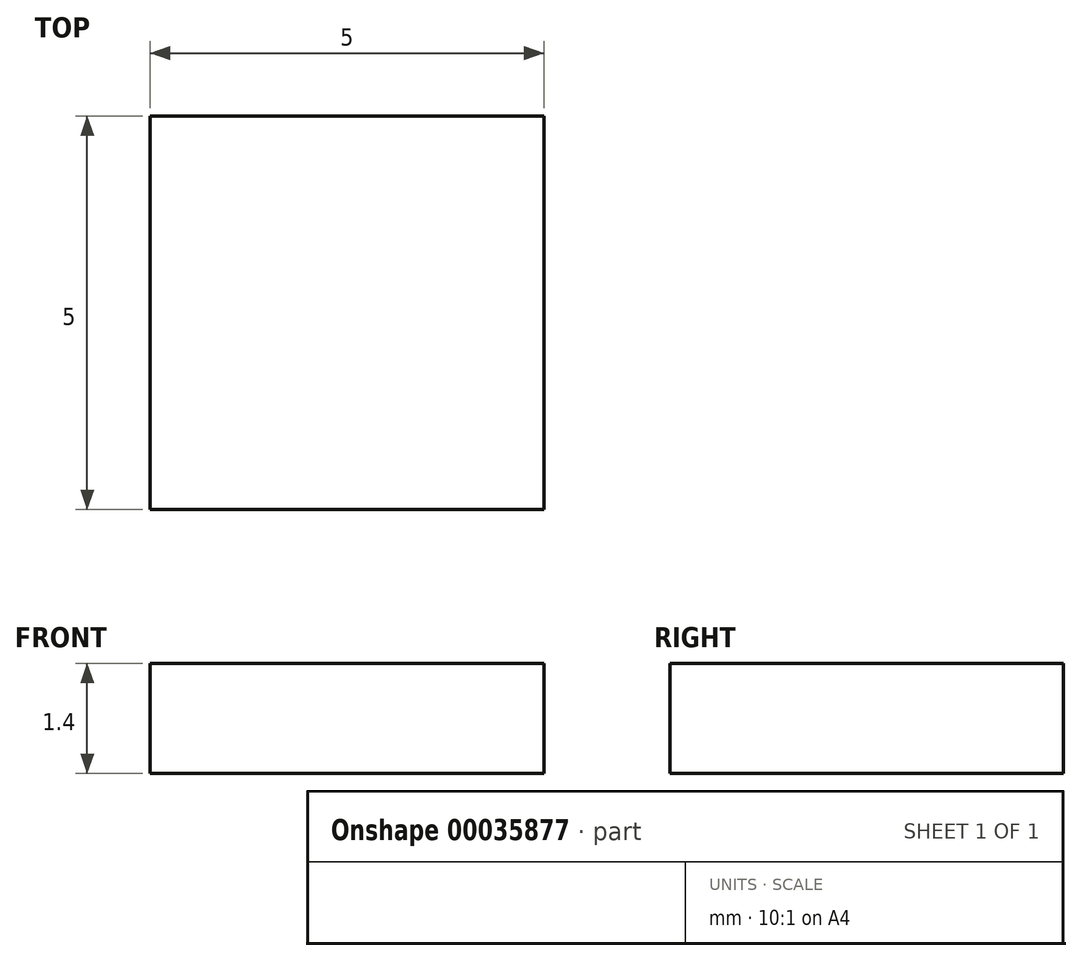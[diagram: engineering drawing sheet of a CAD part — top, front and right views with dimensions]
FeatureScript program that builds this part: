
annotation { "Feature Type Name" : "Feature", "Feature Type Description" : "" }
export const myFeature = defineFeature(function(context is Context, id is Id, definition is map)
    precondition{}
    {
        {
            var Q0;
            Q0=qCreatedBy(makeId("Top.planeOp"),FACE);
            var sketch = newSketch(context, id + "F0", { "sketchPlane" : qUnion([Q0])});
            skLineSegment(sketch, "E0.bottom", {"start": v(0, 0) * mm, "end": v(5, 0) * mm});
            skLineSegment(sketch, "E0.top", {"start": v(0, -5) * mm, "end": v(5, -5) * mm});
            skLineSegment(sketch, "E0.left", {"start": v(0, 0) * mm, "end": v(0, -5) * mm});
            skLineSegment(sketch, "E0.right", {"start": v(5, 0) * mm, "end": v(5, -5) * mm});
            skSolve(sketch);
        }
        {
            var Q0;
            Q0=makeQuery(id+"F0.imprint","IMPRINT",FACE,{"disambiguationData":[TD([[makeQuery(id+"F0.imprint","IMPRINT",EDGE,{"derivedFrom":sQuery(id+"F0.wireOp",EDGE,"E0.bottom")}),-1.0]])]});
            extrude(context, id + "F1", {"entities" : qUnion([Q0]), "depth" : 1.4 * mm});
        }
    });
